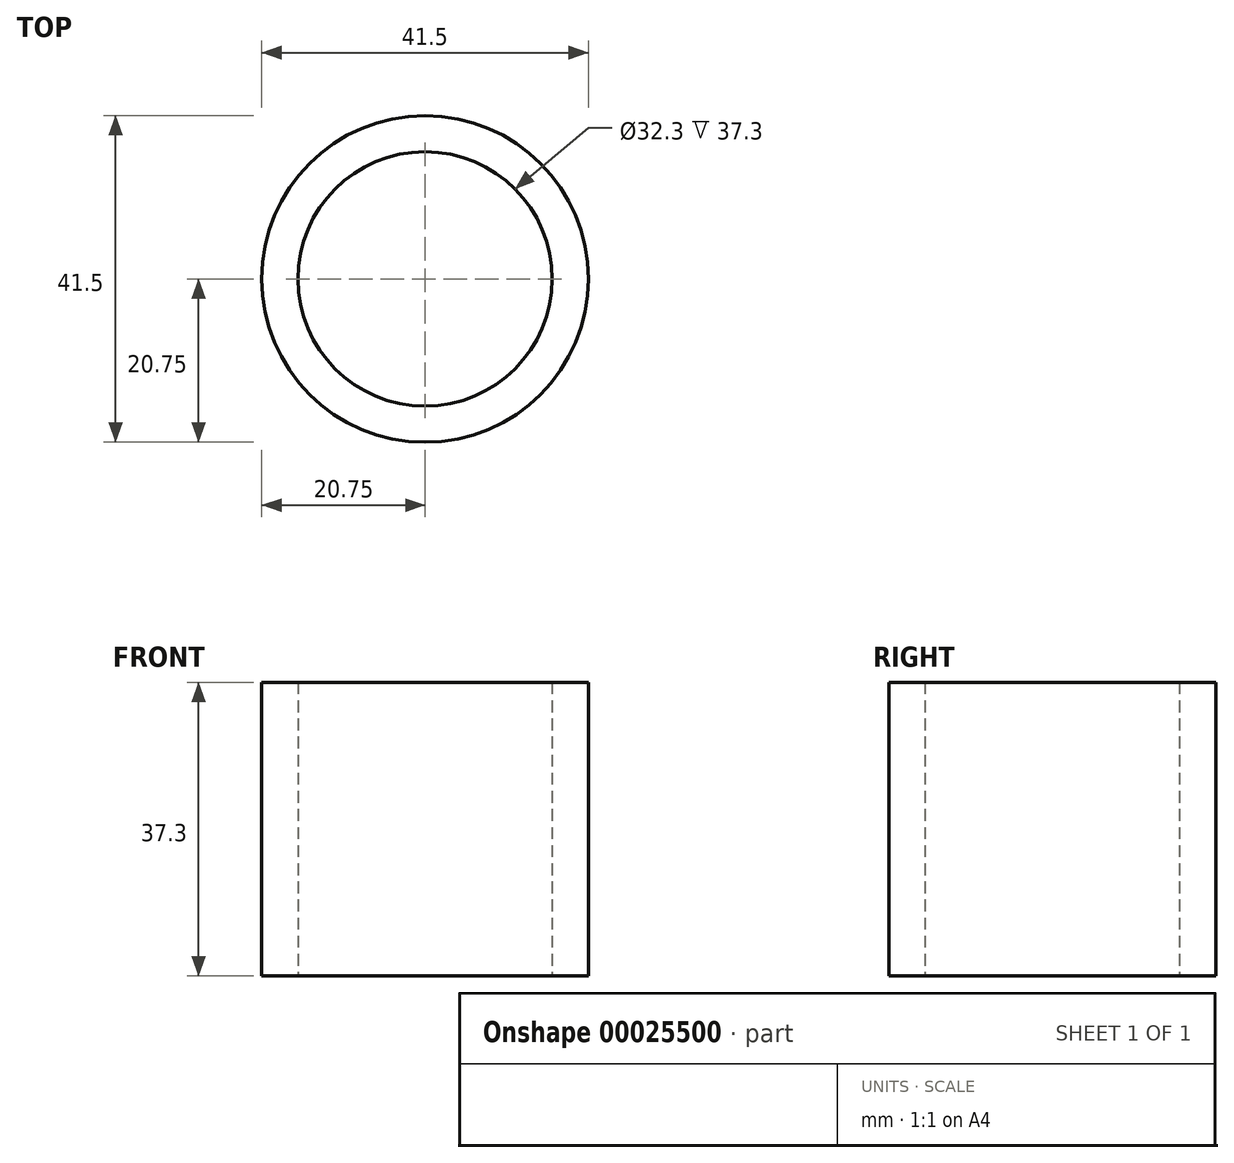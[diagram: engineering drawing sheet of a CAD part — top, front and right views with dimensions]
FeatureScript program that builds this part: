
annotation { "Feature Type Name" : "Feature", "Feature Type Description" : "" }
export const myFeature = defineFeature(function(context is Context, id is Id, definition is map)
    precondition{}
    {
        {
            var Q0;
            Q0=qCreatedBy(makeId("Top.planeOp"),FACE);
            var sketch = newSketch(context, id + "F0", { "sketchPlane" : qUnion([Q0])});
            skCircle(sketch, "E0", {"center": v(0, 0) * mm, "radius": 20.75 * mm});
            skCircle(sketch, "E1", {"center": v(0, 0) * mm, "radius": 16.15 * mm});
            skSolve(sketch);
        }
        {
            var Q0;
            Q0=makeQuery(id+"F0.imprint","IMPRINT",FACE,{"disambiguationData":[TD([[makeQuery(id+"F0.imprint","IMPRINT",EDGE,{"derivedFrom":sQuery(id+"F0.wireOp",EDGE,"E0")}),1.0]])]});
            extrude(context, id + "F1", {"entities" : qUnion([Q0]), "depth" : 37.3 * mm});
        }
    });
